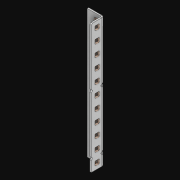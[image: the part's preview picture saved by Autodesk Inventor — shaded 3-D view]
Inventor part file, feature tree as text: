
AUTODESK INVENTOR PART (.ipt)
format: ipt  version: 2021 (Build 250183000, 183)  size: 1,124,352 bytes
history: native  units: in
note: dims shown in document units (in); Inventor stores cm internally (conversion verified against a paired STEP export)
features: extrude x24, other x22, sketch x4, pattern_linear x2, sheet_metal_op x1
ambient origin geometry x8: Origin, YZ Plane, XZ Plane, XY Plane, X Axis, Y Axis, Z Axis, Center Point
bodies: Solid1 (feature_tree)
feature tree (53):
  pattern_linear  "Rectangular Pattern1"  Spacing1=0.5in  [1 undecoded]
  pattern_linear  "Rectangular Pattern3"  Count1=11  [1 undecoded]
  extrude  "Extrusion1"  Depth=0.5in
  extrude  "Extrusion2"  Depth=0.5in
  sketch  "Sketch1"  dims[d0=0.182in]
  other  "Srf1"
  sketch  "Sketch3"  dims[d1=0.063in d2=0.0in]
  other  "Srf3"
  other  "Srf4"
  other  "Srf5"
  other  "Srf6"
  other  "Srf7"
  other  "Srf8"
  other  "Srf9"
  other  "Srf10"
  other  "Srf11"
  other  "Srf12"
  other  "Srf13"
  other  "Srf142"
  other  "Srf143"
  other  "Srf144"
  other  "Srf145"
  other  "Srf146"
  other  "Srf147"
  other  "Srf148"
  other  "Srf149"
  other  "Srf150"
  other  "Srf151"
  sketch  "Sketch4"  dims[d6=0.182in]
  sketch  "Sketch5"  dims[d7=0.063in d8=0.0in d11=0.5in d12=0.3937in d14=0.5in d18=4.3307in d20=0.5in d21=12.0in d22=0.0in d23=0.841in d24=0.0in]
  sheet_metal_op  "Fold1"
  extrude  "ExtrusionSrf1"  TaperAngle=0.0deg  [1 undecoded]
  extrude  "ExtrusionSrf3"  Depth=0.5in TaperAngle=0.0deg
  extrude  "ExtrusionSrf4"  [1 undecoded]
  extrude  "ExtrusionSrf5"  [1 undecoded]
  extrude  "ExtrusionSrf6"  [1 undecoded]
  extrude  "ExtrusionSrf7"  [1 undecoded]
  extrude  "ExtrusionSrf8"  [1 undecoded]
  extrude  "ExtrusionSrf9"  [1 undecoded]
  extrude  "ExtrusionSrf10"  [1 undecoded]
  extrude  "ExtrusionSrf11"  [1 undecoded]
  extrude  "ExtrusionSrf12"  [1 undecoded]
  extrude  "ExtrusionSrf13"  [1 undecoded]
  extrude  "ExtrusionSrf142"  [1 undecoded]
  extrude  "ExtrusionSrf143"  [1 undecoded]
  extrude  "ExtrusionSrf144"  [1 undecoded]
  extrude  "ExtrusionSrf145"  [1 undecoded]
  extrude  "ExtrusionSrf146"  [1 undecoded]
  extrude  "ExtrusionSrf147"  [1 undecoded]
  extrude  "ExtrusionSrf148"  [1 undecoded]
  extrude  "ExtrusionSrf149"  [1 undecoded]
  extrude  "ExtrusionSrf150"  [1 undecoded]
  extrude  "ExtrusionSrf151"  [1 undecoded]
note: 23 required parameter values undecoded (feature->parameter linkage not recoverable at this tier; creation-order binding heuristic only, values carry confidence <= 0.55)
